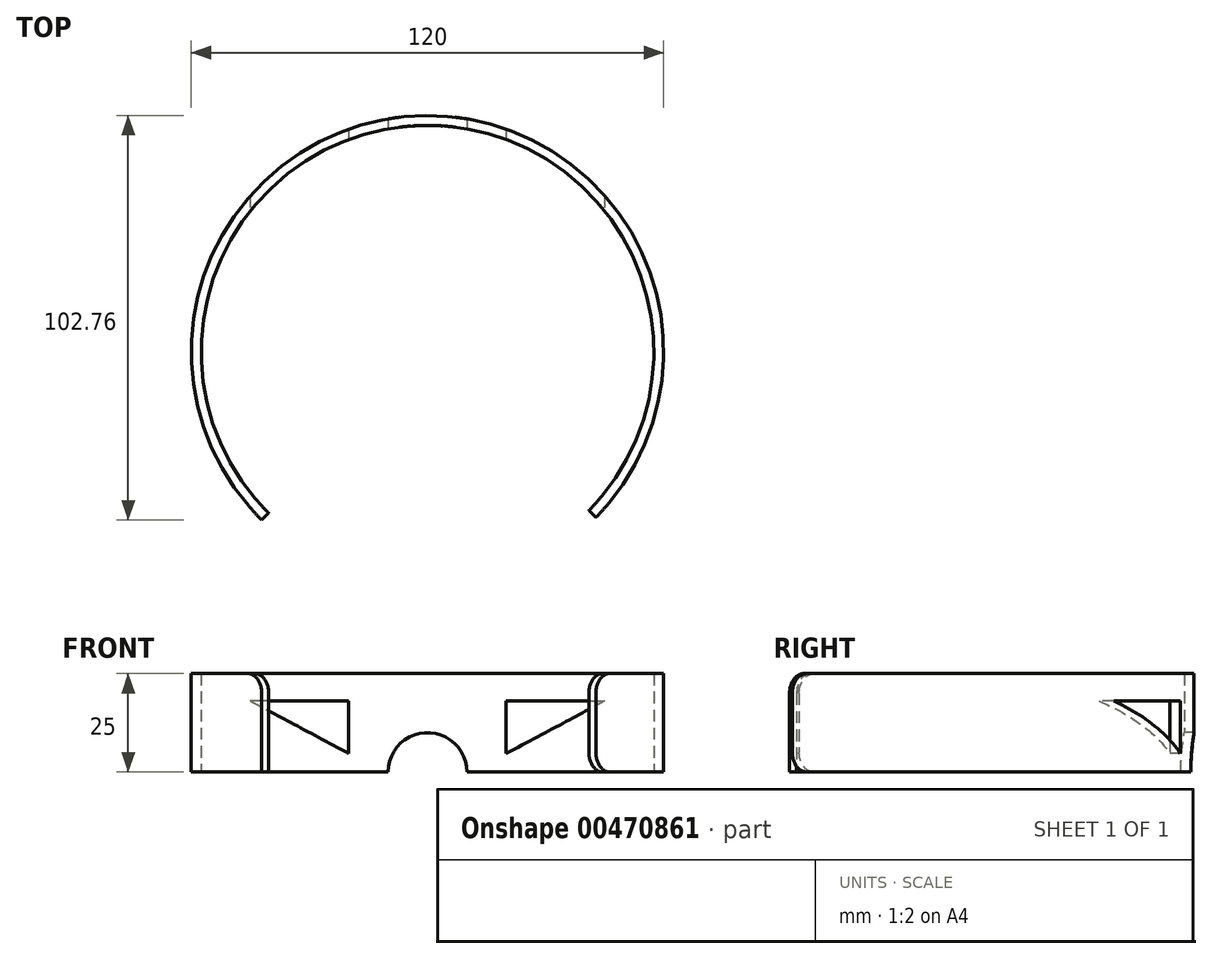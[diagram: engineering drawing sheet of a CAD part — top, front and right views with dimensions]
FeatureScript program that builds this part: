
annotation { "Feature Type Name" : "Feature", "Feature Type Description" : "" }
export const myFeature = defineFeature(function(context is Context, id is Id, definition is map)
    precondition{}
    {
        {
            var Q0;
            Q0=qCreatedBy(makeId("Top.planeOp"),FACE);
            var sketch = newSketch(context, id + "F0", { "sketchPlane" : qUnion([Q0])});
            skCircle(sketch, "E0", {"center": v(0, 0) * mm, "radius": 60 * mm});
            skCircle(sketch, "E1", {"center": v(0, 0) * mm, "radius": 57.5 * mm});
            skSolve(sketch);
        }
        {
            var Q0;
            Q0=makeQuery(id+"F0.imprint","IMPRINT",FACE,{"disambiguationData":[TD([[makeQuery(id+"F0.imprint","IMPRINT",EDGE,{"derivedFrom":sQuery(id+"F0.wireOp",EDGE,"HNiywZih-IFeU-TFh5-rXyx-FrnGBEJkzCFk")}),-1.0]])]});
            var Q1;
            Q1=makeQuery(id+"F0.imprint","IMPRINT",FACE,{"disambiguationData":[TD([[makeQuery(id+"F0.imprint","IMPRINT",EDGE,{"derivedFrom":sQuery(id+"F0.wireOp",EDGE,"E0")}),1.0]])]});
            extrude(context, id + "F1", {"entities" : qUnion([Q0, Q1]), "depth" : 25 * mm});
        }
        {
            var Q0;
            Q0=qCreatedBy(makeId("Front.planeOp"),FACE);
            var sketch = newSketch(context, id + "F2", { "sketchPlane" : qUnion([Q0])});
            skCircle(sketch, "E2", {"center": v(0, 0) * mm, "radius": 10 * mm});
            skSolve(sketch);
        }
        {
            var Q0;
            Q0=makeQuery(id+"F2.imprint","IMPRINT",FACE,{"disambiguationData":[TD([[makeQuery(id+"F2.imprint","IMPRINT",EDGE,{"derivedFrom":sQuery(id+"F2.wireOp",EDGE,"E2")}),1.0]])]});
            extrude(context, id + "F3", {"entities" : qUnion([Q0]), "operationType" : NewBodyOperationType.REMOVE, "endBound" : BoundingType.THROUGH_ALL, "oppositeDirection" : true, "depth" : 25 * mm});
        }
        {
            var Q0;
            Q0=qCreatedBy(makeId("Front.planeOp"),FACE);
            var sketch = newSketch(context, id + "F4", { "sketchPlane" : qUnion([Q0])});
            skLineSegment(sketch, "E3", {"start": v(20, 18.04) * mm, "end": v(45.02, 18.04) * mm});
            skLineSegment(sketch, "E4", {"start": v(45.02, 18.04) * mm, "end": v(20, 4.66) * mm});
            skLineSegment(sketch, "E5", {"start": v(20, 18.04) * mm, "end": v(20, 4.66) * mm});
            skLineSegment(sketch, "E6.MirrorCS", {"start": v(-20, 18.04) * mm, "end": v(-45.02, 18.04) * mm});
            skLineSegment(sketch, "E7.MirrorCS", {"start": v(-45.02, 18.04) * mm, "end": v(-20, 4.66) * mm});
            skLineSegment(sketch, "E8.MirrorCS", {"start": v(-20, 18.04) * mm, "end": v(-20, 4.66) * mm});
            skSolve(sketch);
        }
        {
            var Q0;
            Q0=makeQuery(id+"F4.imprint","IMPRINT",FACE,{"disambiguationData":[TD([[makeQuery(id+"F4.imprint","IMPRINT",EDGE,{"derivedFrom":sQuery(id+"F4.wireOp",EDGE,"E6.MirrorCS")}),1.0]])]});
            var Q1;
            Q1=makeQuery(id+"F4.imprint","IMPRINT",FACE,{"disambiguationData":[TD([[makeQuery(id+"F4.imprint","IMPRINT",EDGE,{"derivedFrom":sQuery(id+"F4.wireOp",EDGE,"E3")}),-1.0]])]});
            extrude(context, id + "F5", {"entities" : qUnion([Q0, Q1]), "operationType" : NewBodyOperationType.REMOVE, "endBound" : BoundingType.THROUGH_ALL, "oppositeDirection" : true, "depth" : 25 * mm});
        }
        {
            var Q0;
            Q0=qCreatedBy(makeId("Top.planeOp"),FACE);
            var sketch = newSketch(context, id + "F6", { "sketchPlane" : qUnion([Q0])});
            skLineSegment(sketch, "E9", {"start": v(0, 0) * mm, "end": v(-63.99, -65) * mm});
            skLineSegment(sketch, "E10", {"start": v(-63.99, -65) * mm, "end": v(66.01, -65) * mm});
            skLineSegment(sketch, "E11", {"start": v(66.01, -65) * mm, "end": v(0, 0) * mm});
            skSolve(sketch);
        }
        {
            var Q0;
            Q0=makeQuery(id+"F6.imprint","IMPRINT",FACE,{"disambiguationData":[TD([[makeQuery(id+"F6.imprint","IMPRINT",EDGE,{"derivedFrom":sQuery(id+"F6.wireOp",EDGE,"E9")}),1.0]])]});
            extrude(context, id + "F7", {"entities" : qUnion([Q0]), "operationType" : NewBodyOperationType.REMOVE, "endBound" : BoundingType.THROUGH_ALL, "depth" : 25 * mm});
        }
        {
            var Q0;
            Q0=makeQuery(id+"F7.boolean.opBoolean","INTERSECT",EDGE,{"derivedFrom":[makeQuery(id+"F1.opExtrude","CAP_FACE",FACE,{"disambiguationData":[OSD([sQuery(id+"F0.wireOp",EDGE,"E0"),sQuery(id+"F0.wireOp",EDGE,"E1")])],"isStart":false}),makeQuery(id+"F7.opExtrude","SWEPT_FACE",FACE,{"disambiguationData":[OSD([sQuery(id+"F6.wireOp",EDGE,"E9")])]})]});
            var Q1;
            Q1=makeQuery(id+"F7.boolean.opBoolean","COPY",EDGE,{"derivedFrom":makeQuery(id+"F7.opExtrude","CAP_EDGE",EDGE,{"disambiguationData":[OSD([sQuery(id+"F6.wireOp",EDGE,"E9")])],"isStart":true})});
            var Q2;
            Q2=makeQuery(id+"F7.boolean.opBoolean","INTERSECT",EDGE,{"derivedFrom":[makeQuery(id+"F1.opExtrude","CAP_FACE",FACE,{"disambiguationData":[OSD([sQuery(id+"F0.wireOp",EDGE,"E0"),sQuery(id+"F0.wireOp",EDGE,"E1")])],"isStart":false}),makeQuery(id+"F7.opExtrude","SWEPT_FACE",FACE,{"disambiguationData":[OSD([sQuery(id+"F6.wireOp",EDGE,"E11")])]})]});
            var Q3;
            Q3=makeQuery(id+"F7.boolean.opBoolean","COPY",EDGE,{"derivedFrom":makeQuery(id+"F7.opExtrude","CAP_EDGE",EDGE,{"disambiguationData":[OSD([sQuery(id+"F6.wireOp",EDGE,"E11")])],"isStart":true})});
            fillet(context, id + "F8", {"entities" : qUnion([Q0, Q1, Q2, Q3]), "radius" : 5 * mm, "tangentPropagation" : true, "allowEdgeOverflow" : false});
        }
    });
